# Revit family: QF_ELECTROLUXPROFESSIONAL_1LSNSP_TD6-10_E
name_source: partatom
category: Attrezzature speciali
units: mm (PartAtom-declared; Revit-internal decimal feet)

## family parameters
Basato su piano di lavoro = No
Condiviso = No
Punto di calcolo locali = No
Quota connettore circolare = Usa diametro
Sempre verticale = Sì
Taglio con vuoti quando caricato = No
Tipo di parte = Normale

## types (35) — shared parameters
Depth Actual = 765 mm  [stored 2.50984 ft]
Height Actual = 1115 mm  [stored 3.65814 ft]
Latent Heat Output = 0.0
Length Actual = 720 mm  [stored 2.3622 ft]
Modello = TD6-10
Produttore = Electrolux Professional
Sensible Heat Output = 0.0
URL = www.electroluxprofessional.com
Weight = 99
zero-valued in all types: Gas KW, Prospetto di default, Steam Pounds per Hour

## per-type parameters (varying)
| type | Cycle | Descrizione | Item Number | Phase | Volts | Watts |
| 9873530045 | 50 Hz | TUMBLE DRYER TD6-10 10KG/23LB SST DRUM EL 8KW 400/50/3N COMPASS PRO 6G81 SST/SLVR DO.RIGHT REV MB DISCON XT.CON | 1LA262 | 3 | 400 V | 8400 W |
| 9873530005 | 50 Hz | TUMBLE DRYER TD6-10 10KG/23LB SST DRUM EL 8KW 400/50/3N COMPASS PRO 6G81 SLVR/SLVR DO.RIGHT REV MB DISCON XT.CON | 1LSP06 | 3 | 400 V | 8400 W |
| 9873530015 | 60 Hz | TUMBLE DRYER TD6-10 MARINE 10KG/23LB SST DRUM EL 8KW 440/60/3 COMPASS PRO 6G81 SLVR/SLVR DO.RIGHT REV MB DISCON | 1LSP0F | 3 | 440 V | 8400 W |
| 9873530040 | 50 Hz | TUMBLE DRYER TD6-10 MARINE 10KG/23LB SST DRUM EL 8KW 415/50/3 COMPASS PRO 6G81 SST/SLVR DO.LEFT REV MB STOP DISCON | 1L0GZC | 3 | 415 V | 8400 W |
| 9873530010 | 50 Hz | TUMBLE DRYER TD6-10 10KG/23LB GALVA.DRUM EL 8KW 230/50/1N COMPASS PRO 6G81 SLVR/SLVR DO.RIGHT REV MB DISCON XT.CON | 1LSP0B | 1 | 230 V | 8400 W |
| 9873530028 | 60 Hz | TUMBLE DRYER TD6-10 10KG/23LB GALVA.DRUM EL 6KW 230/60/1N COMPASS PRO 6G81 SST/SLVR DO.RIGHT REV MB DISCON XT.CON | 1L0GB1 | 1 | 230 V | 6400 W |
| 9873530038 | 50 Hz | TUMBLE DRYER TD6-10 10KG/23LB SST DRUM EL 6KW 230/50/3 COMPASS PRO 6G82 SLVR/SLVR DO.LEFT REV STOP DISCON | 1LA24N | 3 | 230 V | 6400 W |
| 9873530008 | 60 Hz | TUMBLE DRYER TD6-10 MARINE 10KG/23LB GALVA.DRUM EL 6KW 440/60/3 COMPASS PRO 6G81 SLVR/SLVR DO.RIGHT REV MB DISCON | 1LSP09 | 3 | 440 V | 6400 W |
| 9873530018 | 60 Hz | TUMBLE DRYER TD6-10 10KG/23LB GALVA.DRUM EL 6KW 230/60/3 COMPASS PRO 6G81 SST/SLVR DO.RIGHT REV MB DISCON | 1LSP20 | 3 | 230 V | 6400 W |
| 9873530047 | 60 Hz | TUMBLE DRYER TD6-10 MARINE 10KG SST DRUM EL 8KW 480/60/3 COMPASS PRO 6G81 SST/SLVR DO.RIGHT REV MB STOP DISCON | 1LT6VG | 3 | 480 V | 8400 W |
| 9873530037 | 50 Hz | TUMBLE DRYER TD6-10 10KG/23LB GALVA.DRUM EL 6KW 400/50/3N COMPASS PRO 6G81 SST/SLVR DO.RIGHT REV MB DISCON XT.CON | 1LA24M | 3 | 400 V | 6400 W |
| 9873530007 | 50 Hz | TUMBLE DRYER TD6-10 10KG/23LB GALVA.DRUM EL 8KW 400/50/3N COMPASS PRO 6A81 2.I/O SLVR/SLVR DO.RIGHT PREP.CB REV MB D... | 1LSP08 | 3 | 400 V | 8400 W |
| 9873530017 | 60 Hz | TUMBLE DRYER TD6-10 MARINE 10KG/23LB GALVA.DRUM EL 8KW 440/60/3 COMPASS PRO 6G81 SST/SLVR DO.RIGHT REV MB DISCON | 1LSP0H | 3 | 440 V | 8400 W |
| 9873530042 | 50 Hz | TUMBLE DRYER TD6-10 10KG/23LB GALVA.DRUM EL 8KW 400/50/3N COMPASS PRO 6L80 SLVR/SLVR DO.RIGHT REV DISCON XT.CON | 1L828Y | 3 | 400 V | 8400 W |
| 9873530032 | 60 Hz | TUMBLE DRYER TD6-10 MARINE 10KG/23LB GALVA.DRUM EL 8KW 480/60/3 COMPASS PRO 6G81 SLVR/SLVR DO.LEFT REV MB DISCON | 1L0GFJ | 3 | 480 V | 8400 W |
| 9873530002 | 50 Hz | TUMBLE DRYER TD6-10 10KG/23LB GALVA.DRUM EL 6KW 400/50/3N COMPASS PRO 6G81 SLVR/SLVR DO.RIGHT REV MB DISCON XT.CON | 1LSP04 | 3 | 400 V | 6400 W |
| 9873530012 | 50 Hz | TUMBLE DRYER TD6-10 MARINE 10KG/23LB GALVA.DRUM EL 6KW 400/50/3 COMPASS PRO 6G81 SLVR/SLVR DO.RIGHT REV MB DISCON | 1LSP0D | 3 | 400 V | 6400 W |
| 9873530041 | 50 Hz | TUMBLE DRYER TD6-10 MARINE 10KG/23LB SST DRUM EL 6KW 230/50/1N COMPASS PRO 6G81 SST/SLVR DO.RIGHT REV MB DISCON XT.CON | 1L0GZD | 1 | 230 V | 6400 W |
| 9873530001 | 50 Hz | TUMBLE DRYER TD6-10 10KG/23LB GALVA.DRUM EL 6KW 400/50/3N COMPASS PRO 6A81 SLVR/SLVR DO.LEFT REV MB XT.CON | 1LSNT5 | 3 | 400 V | 6400 W |
| 9873530011 | 50 Hz | TUMBLE DRYER TD6-10 10KG/23LB GALVA.DRUM EL 8KW 400/50/3N COMPASS PRO 6L80 2.I/O SLVR/SLVR DO.RIGHT EXT.PM. REV DISC... | 1LSP0C | 3 | 400 V | 8400 W |
| 9873530039 | 50 Hz | TUMBLE DRYER TD6-10 10KG/23LB SST DRUM EL 6KW 230/50/1N COMPASS PRO 6G81 SLVR/SLVR DO.RIGHT REV MB DISCON XT.CON | 1LSPL2 | 1 | 230 V | 6400 W |
| 9873530009 | 50 Hz | TUMBLE DRYER TD6-10 10KG/23LB GALVA.DRUM EL 8KW 230/50/3 COMPASS PRO 6G81 SLVR/SLVR DO.RIGHT REV MB DISCON | 1LSP0A | 3 | 230 V | 8400 W |
| 9873530019 | 60 Hz | TUMBLE DRYER TD6-10 MARINE 10KG/23LB SST DRUM EL 8KW 440/60/3 COMPASS PRO 6G81 SST/SLVR DO.RIGHT REV MB DISCON | 1LA09Z | 3 | 440 V | 8400 W |
| 9873530044 | 60 Hz | TUMBLE DRYER TD6-10 MARINE 10KG/23LB SST DRUM EL 8KW 208-240/60/3 COMPASS PRO 6G81 SLVR/SLVR DO.RIGHT REV MB STOP DI... | 1LA25T | 3 | 240 V | 8400 W |
| 9873530024 | 50 Hz | TUMBLE DRYER TD6-10 10KG/23LB SST DRUM EL 8KW 400/50/3N COMPASS PRO 6G81 SLVR/SLVR DO.LEFT REV MB STOP DISCON XT.CON | 1LSP4W | 3 | 400 V | 8400 W |
| 9873530034 | 50 Hz | TUMBLE DRYER TD6-10 MARINE 10KG/23LB SST DRUM EL 6KW 230/50/3 COMPASS PRO 6G82 SLVR/SLVR DO.LEFT REV STOP DISCON | 1L0GTM | 3 | 230 V | 6400 W |
| 9873530004 | 50 Hz | TUMBLE DRYER TD6-10 10KG/23LB GALVA.DRUM EL 8KW 400/50/3N COMPASS PRO 6A81 SLVR/SLVR DO.RIGHT ELS-NETW. REV MB DISCO... | 1LSP05 | 3 | 400 V | 8400 W |
| 9873530014 | 50 Hz | TUMBLE DRYER TD6-10 10KG/23LB SST DRUM EL 8KW 400/50/3 COMPASS PRO 6G81 SLVR/SLVR DO.RIGHT REV MB DISCON | 1LSP0E | 3 | 400 V | 8400 W |
| 9873530043 | 60 Hz | TUMBLE DRYER TD6-10 MARINE 10KG/23LB GALVA.DRUM EL 8KW 208-240/60/3 COMPASS PRO 6G81 SST/SLVR DO.RIGHT REV MB DISCON | 1L82B0 | 3 | 240 V | 8400 W |
| 9873530033 | 60 Hz | TUMBLE DRYER TD6-10 MARINE 10KG/23LB GALVA.DRUM EL 6KW 400/60/3N COMPASS PRO 6G82 SLVR/SLVR DO.RIGHT REV STOP DISCON... | 1LSPDB | 3 | 400 V | 6400 W |
| 9873530003 | 50 Hz | TUMBLE DRYER TD6-10 10KG/23LB GALVA.DRUM EL 8KW 400/50/3N COMPASS PRO 6G81 SLVR/SLVR DO.RIGHT REV MB DISCON XT.CON | 1LSP0N | 3 | 400 V | 8400 W |
| 9873530013 | 50 Hz | TUMBLE DRYER TD6-10 MARINE 10KG/23LB SST DRUM EL 8KW 400/50/3 COMPASS PRO 6G81 SLVR/SLVR DO.RIGHT REV MB DISCON | 1L0HE0 | 3 | 400 V | 8400 W |
| 9873530036 | 50 Hz | TUMBLE DRYER TD6-10 10KG/23LB GALVA.DRUM EL 8KW 400/50/3N COMPASS PRO 6L80 SLVR/SLVR DO.RIGHT REV XT.CON | 1L0GUU | 3 | 400 V | 8400 W |
| 9873530006 | 50 Hz | TUMBLE DRYER TD6-10 10KG/23LB GALVA.DRUM EL 6KW 230/50/1N COMPASS PRO 6G81 SLVR/SLVR DO.RIGHT REV MB DISCON XT.CON | 1LSP07 | 1 | 230 V | 6400 W |
| 9873530016 | 60 Hz | TUMBLE DRYER TD6-10 MARINE 10KG/23LB GALVA.DRUM EL 4,4KW 115/60/3 COMPASS PRO 6G81 SLVR/SLVR DO.RIGHT REV MB DISCON | 1LSP0G | 3 | 115 V | 4500 W |

note: [stored X ft] marks values corroborated as IEEE doubles in the binary element streams (Revit-internal decimal feet)

## geometry (parser evidence)
native form markers: Blend x8
no freeform markers — native parametric forms only
